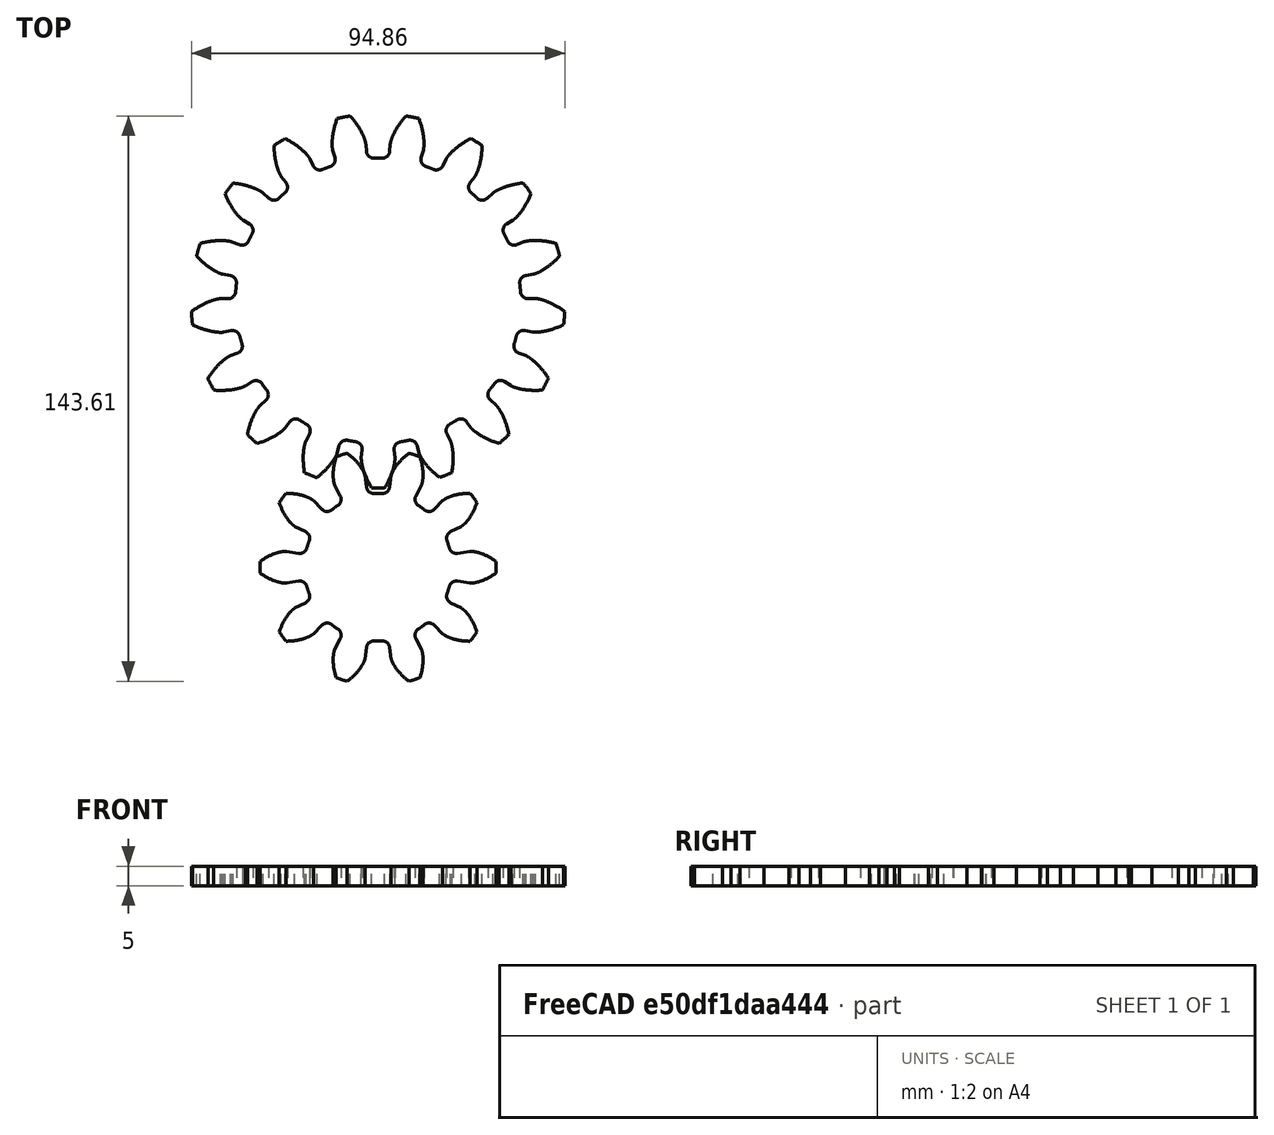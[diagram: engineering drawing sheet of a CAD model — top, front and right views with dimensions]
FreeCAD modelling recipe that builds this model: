
FCSTD DOCUMENT  (FreeCAD 0.20R29177 +426 (Git))
Label: Engranaje parametrizado
License: All rights reserved
LicenseURL: http://en.wikipedia.org/wiki/All_rights_reserved
objects: Part::Part2DObjectPython×2, PartDesign::Pad×2, PartDesign::Body×2, Spreadsheet::Sheet×1
note: 8 computed .brp shape members not serialized (recipe doc carries the construction recipe); baked Part::Feature solids carry a one-line shape summary decoded from their .brp

FEATURE [Spreadsheet::Sheet] Spreadsheet  label="Medidas"
  cells = A1=Velocidad nominal de rotacion engranaje conducido(ne); B1(ne)=25; A2=Velocidad nominal de rotacion engranaje motriz (ns); B2(ns)=15; A3=Espesor; B3(espesor)=5; A4=Diémetro Primitivo (Dp); B4(Dp)=50; A5=No. dientes (z); B5(z)=10; A6=eje1; B6(eje1)=15; A7=eje2; B7(eje2)=15; A9=DATOS OBTENIDOS ; A10=Módulo (m); B10==B4 / B5; A11=Relación de transmisión (i); B11==B2 / B1; A12=No. dientes del engranaje conducido (z2); B12==B5 / B11; A13=Diametro Primitivo engranaje conducido (Dp); B13==B12 * B10; A14=Distancia entre ejes ; B14(ejesDist)==B4 / 2 + B13 / 2
FEATURE [Part::Part2DObjectPython] InvoluteGear  # Draft 2D object (typed FeaturePython)
  ExternalGear = true
  HighPrecision = true
  Modules = 5
  NumberOfTeeth = 10
  PressureAngle = 20
  expr: Modules = <<Medidas>>.Dp / <<Medidas>>.z
  expr: NumberOfTeeth = Spreadsheet.z
FEATURE [Part::Part2DObjectPython] InvoluteGear001  # Draft 2D object (typed FeaturePython)
  ExternalGear = true
  HighPrecision = true
  Modules = 5
  NumberOfTeeth = 17
  PressureAngle = 20
  expr: Modules = <<Medidas>>.Dp / <<Medidas>>.z
  expr: NumberOfTeeth = <<Medidas>>.z / (<<Medidas>>.ns / <<Medidas>>.ne)
FEATURE [PartDesign::Pad] Pad
  Direction = (0,0,1)
  Length = 5
  Length2 = 10
  Profile = -> InvoluteGear
  ReferenceAxis = -> InvoluteGear [N_Axis]
  Type = 0
  expr: Length = <<Medidas>>.espesor
FEATURE [PartDesign::Body] Body  label="Motriz"
  Group = -> [InvoluteGear,Pad]
  Origin = -> Origin
  Tip = -> Pad
FEATURE [PartDesign::Pad] Pad001
  Direction = (0,0,1)
  Length = 5
  Length2 = 10
  Profile = -> InvoluteGear001
  ReferenceAxis = -> InvoluteGear001 [N_Axis]
  Type = 0
  expr: Length = <<Medidas>>.espesor
FEATURE [PartDesign::Body] Body001  label="Conducido"
  Group = -> [InvoluteGear001,Pad001]
  Origin = -> Origin001
  Placement = pos=(0,67.67,0) rot=(0,0,1;0.277507rad)
  Tip = -> Pad001
  expr: .Placement.Base.y = <<Medidas>>.ejesDist + 1
